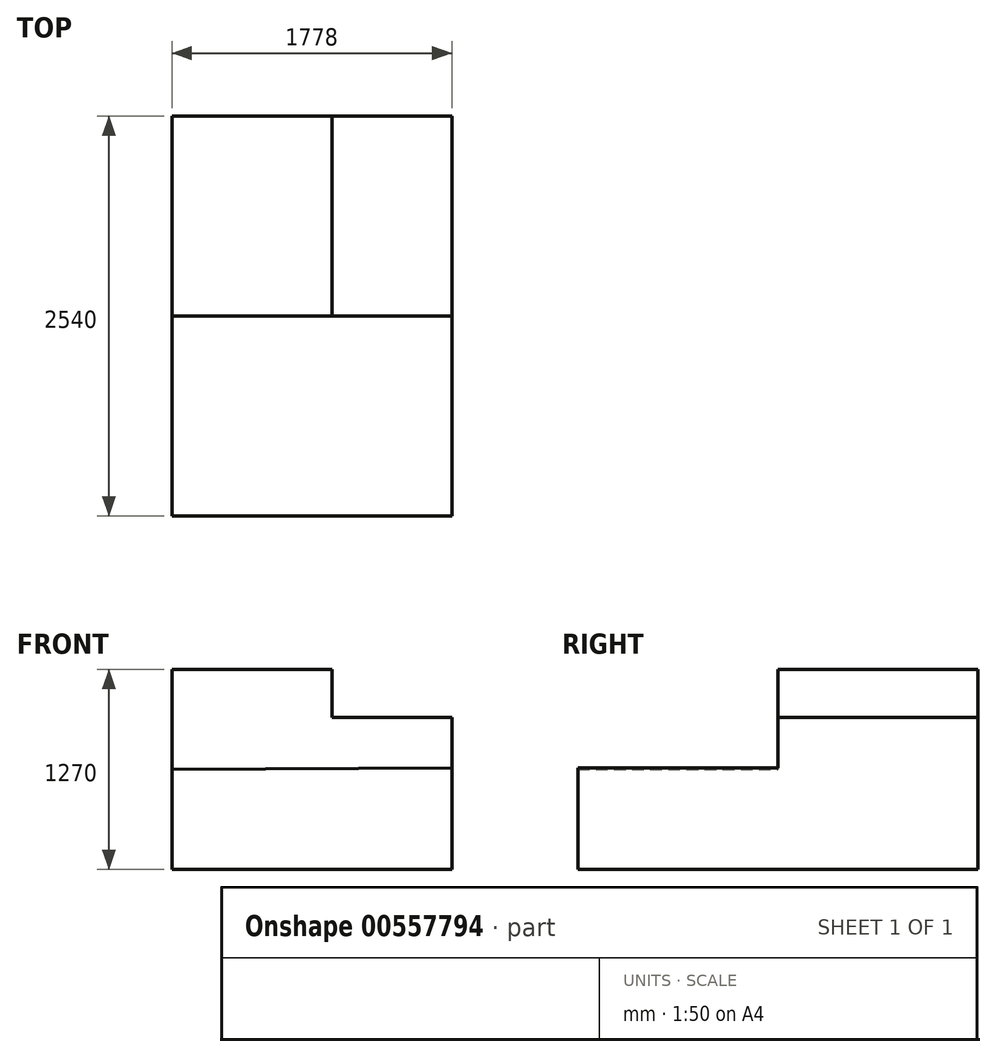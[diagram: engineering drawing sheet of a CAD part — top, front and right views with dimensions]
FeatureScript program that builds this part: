
annotation { "Feature Type Name" : "Feature", "Feature Type Description" : "" }
export const myFeature = defineFeature(function(context is Context, id is Id, definition is map)
    precondition{}
    {
        {
            var Q0;
            Q0=qCreatedBy(makeId("Front.planeOp"),FACE);
            var sketch = newSketch(context, id + "F0", { "sketchPlane" : qUnion([Q0])});
            skLineSegment(sketch, "E0", {"start": v(-75.73, 677.96) * mm, "end": v(-75.73, 42.96) * mm});
            skLineSegment(sketch, "E1", {"start": v(-75.73, 42.96) * mm, "end": v(1702.27, 42.96) * mm});
            skLineSegment(sketch, "E2", {"start": v(1702.27, 42.96) * mm, "end": v(1702.27, 687.16) * mm});
            skLineSegment(sketch, "E3", {"start": v(1702.27, 687.16) * mm, "end": v(-75.73, 677.96) * mm});
            skSolve(sketch);
        }
        {
            var Q0;
            Q0=makeQuery(id+"F0.imprint","IMPRINT",FACE,{"disambiguationData":[TD([[makeQuery(id+"F0.imprint","IMPRINT",EDGE,{"derivedFrom":sQuery(id+"F0.wireOp",EDGE,"E0")}),1.0]])]});
            extrude(context, id + "F1", {"entities" : qUnion([Q0]), "depth" : 1270 * mm, "offsetDistance" : 25.4 * mm});
        }
        {
            var Q0;
            Q0=makeQuery(id+"F1.opExtrude","SWEPT_FACE",FACE,{"disambiguationData":[OSD([sQuery(id+"F0.wireOp",EDGE,"E2")])]});
            var sketch = newSketch(context, id + "F2", { "sketchPlane" : qUnion([Q0])});
            skLineSegment(sketch, "E4", {"start": v(0, 42.96) * mm, "end": v(1270, 42.96) * mm});
            skLineSegment(sketch, "E5", {"start": v(1270, 42.96) * mm, "end": v(1270, 1008.16) * mm});
            skLineSegment(sketch, "E6", {"start": v(1270, 1008.16) * mm, "end": v(0, 1008.16) * mm});
            skLineSegment(sketch, "E7", {"start": v(0, 1008.16) * mm, "end": v(0, 42.96) * mm});
            skSolve(sketch);
        }
        {
            var Q0;
            {var subQ4=sQuery(id+"F2.wireOp",EDGE,"E4");Q0=makeQuery(id+"F2.imprint","IMPRINT",FACE,{"disambiguationData":[TD([[makeQuery(id+"F2.imprint","IMPRINT",EDGE,{"derivedFrom":subQ4}),1.0]])]});}
            extrude(context, id + "F3", {"entities" : qUnion([Q0]), "operationType" : NewBodyOperationType.ADD, "oppositeDirection" : true, "depth" : 1778 * mm, "offsetDistance" : 25.4 * mm});
        }
        {
            var Q0;
            Q0=makeQuery(id+"F3.boolean.opBoolean","MERGE",FACE,{"derivedFrom":[makeQuery(id+"F1.opExtrude","SWEPT_FACE",FACE,{"disambiguationData":[OSD([sQuery(id+"F0.wireOp",EDGE,"E0")])]}),makeQuery(id+"F3.opExtrude","CAP_FACE",FACE,{"disambiguationData":[OSD([sQuery(id+"F2.wireOp",EDGE,"E4"),sQuery(id+"F2.wireOp",EDGE,"E5"),sQuery(id+"F2.wireOp",EDGE,"E6"),sQuery(id+"F2.wireOp",EDGE,"E7")])],"isStart":false})]});
            var sketch = newSketch(context, id + "F4", { "sketchPlane" : qUnion([Q0])});
            skLineSegment(sketch, "E8", {"start": v(-1270, 1008.16) * mm, "end": v(-1270, 1312.96) * mm});
            skLineSegment(sketch, "E9", {"start": v(-1270, 1312.96) * mm, "end": v(0, 1312.96) * mm});
            skLineSegment(sketch, "E10", {"start": v(0, 1312.96) * mm, "end": v(0, 1008.16) * mm});
            skLineSegment(sketch, "E11", {"start": v(0, 1008.16) * mm, "end": v(-1270, 1008.16) * mm});
            skSolve(sketch);
        }
        {
            var Q0;
            Q0=makeQuery(id+"F4.imprint","IMPRINT",FACE,{"disambiguationData":[TD([[makeQuery(id+"F4.imprint","IMPRINT",EDGE,{"derivedFrom":sQuery(id+"F4.wireOp",EDGE,"E8")}),-1.0]])]});
            extrude(context, id + "F5", {"entities" : qUnion([Q0]), "operationType" : NewBodyOperationType.ADD, "oppositeDirection" : true, "depth" : 1016 * mm, "offsetDistance" : 25.4 * mm});
        }
    });
